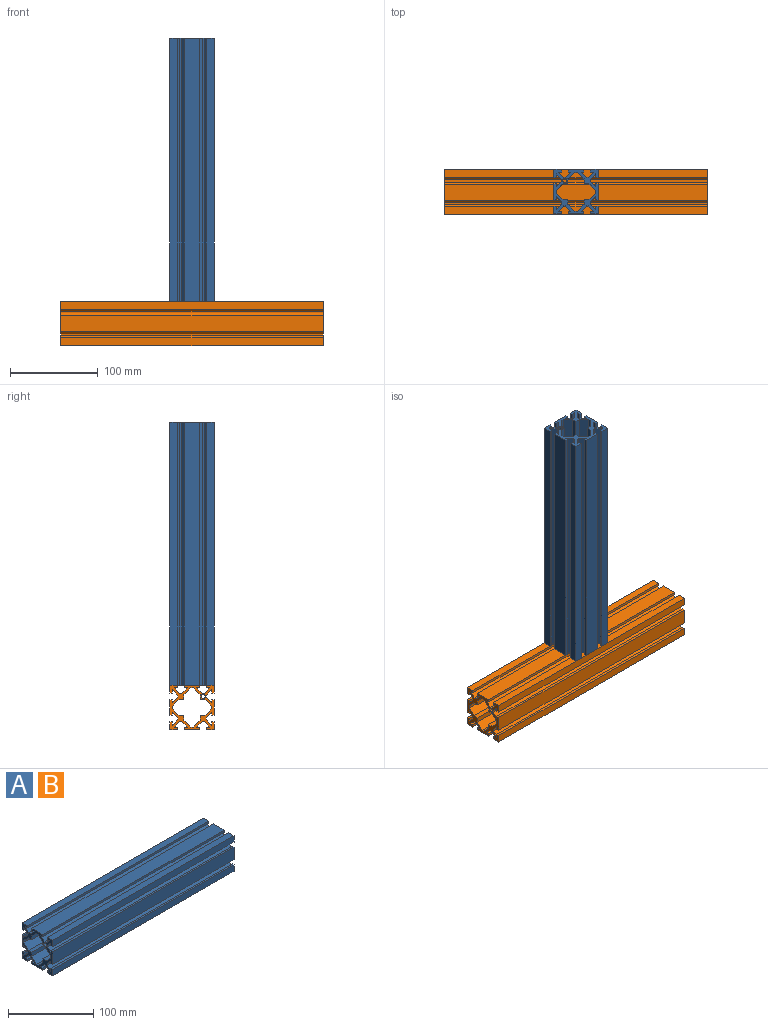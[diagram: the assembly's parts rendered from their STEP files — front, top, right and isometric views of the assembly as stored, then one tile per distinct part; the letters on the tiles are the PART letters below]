
ASSEMBLY  parts=2 mates=2
PART A: 91 faces, bbox 300x50.8x50.8 mm
  f0: plane 300x5.58mm, normal (0,1,0), area 1674mm2, adj f1,f23,f24,f25
  f1: plane 300x7.66mm, normal (0,0.71,-0.71), area 3249.9mm2, adj f0,f2,f24,f25
  f2: plane 300x3mm, normal (0,0,-1), area 900mm2, adj f1,f24,f25,f49
  f3: plane 300x18mm, normal (0,0,1), area 5400mm2, adj f4,f24,f25,f50
  f4: plane 300x3mm, normal (0,-1,0), area 900mm2, adj f3,f5,f24,f25
  f5: plane 300x3.52mm, normal (0,0,-1), area 1056.2mm2, adj f4,f6,f24,f25
  f6: plane 300x6.16mm, normal (0,-0.71,0.71), area 2613.5mm2, adj f5,f7,f24,f25
  f7: plane 300x2.48mm, normal (0,0,1), area 743.8mm2, adj f6,f8,f24,f25
  f8: plane 300x6.16mm, normal (0,0.71,0.71), area 2613.5mm2, adj f7,f9,f24,f25
  f9: plane 300x3.88mm, normal (0,0,-1), area 1163.6mm2, adj f8,f10,f24,f25
  f10: plane 300x3mm, normal (0,1,0), area 900mm2, adj f9,f11,f24,f25
  f11: plane 300x9mm, normal (0,0,1), area 2700mm2, adj f10,f12,f24,f25
  f12: plane 300x9mm, normal (0,-1,0), area 2700mm2, adj f11,f13,f24,f25
  f13: plane 300x3mm, normal (0,0,-1), area 900mm2, adj f12,f14,f24,f25
  f14: plane 300x3.88mm, normal (0,1,0), area 1163.6mm2, adj f13,f15,f24,f25
  f15: plane 300x6.16mm, normal (0,-0.71,-0.71), area 2613.5mm2, adj f14,f16,f24,f25
  f16: plane 300x2.22mm, normal (0,-1,0), area 664.8mm2, adj f15,f17,f24,f25
  f17: plane 300x6.16mm, normal (0,-0.71,0.71), area 2613.5mm2, adj f16,f18,f24,f25
  f18: plane 300x3.26mm, normal (0,1,0), area 977.2mm2, adj f17,f19,f24,f25
  f19: plane 300x3mm, normal (0,0,1), area 900mm2, adj f18,f20,f24,f25
  f20: plane 300x18mm, normal (0,-1,0), area 5400mm2, adj f19,f24,f25,f45
  f21: plane 300x3mm, normal (0,1,0), area 900mm2, adj f22,f24,f25,f46
  f22: plane 300x7.66mm, normal (0,0.71,-0.71), area 3249.9mm2, adj f21,f23,f24,f25
  f23: plane 300x5.58mm, normal (0,0,-1), area 1674mm2, adj f0,f22,f24,f25
  f24: plane 50.8x50.8mm, normal (1,0,0), area 894.8mm2, adj f0,f1,f2,f3,f4,f5,f6,f7
  f25: plane 50.8x50.8mm, normal (-1,0,0), area 894.8mm2, adj f0,f1,f2,f3,f4,f5,f6,f7
  f26: plane 300x5.58mm, normal (0,1,0), area 1674mm2, adj f24,f25,f27,f47
  f27: plane 300x7.66mm, normal (0,0.71,0.71), area 3249.9mm2, adj f24,f25,f26,f28
  f28: plane 300x3mm, normal (0,0,1), area 900mm2, adj f24,f25,f27,f71
  f29: plane 300x18mm, normal (0,0,-1), area 5400mm2, adj f24,f25,f30,f72
  f30: plane 300x3mm, normal (0,-1,0), area 900mm2, adj f24,f25,f29,f31
  f31: plane 300x3.52mm, normal (0,0,1), area 1056.2mm2, adj f24,f25,f30,f32
  f32: plane 300x6.16mm, normal (0,-0.71,-0.71), area 2613.5mm2, adj f24,f25,f31,f33
  f33: plane 300x2.48mm, normal (0,0,-1), area 743.8mm2, adj f24,f25,f32,f34
  f34: plane 300x6.16mm, normal (0,0.71,-0.71), area 2613.5mm2, adj f24,f25,f33,f35
  f35: plane 300x3.88mm, normal (0,0,1), area 1163.6mm2, adj f24,f25,f34,f36
  f36: plane 300x3mm, normal (0,1,0), area 900mm2, adj f24,f25,f35,f37
  f37: plane 300x9mm, normal (0,0,-1), area 2700mm2, adj f24,f25,f36,f38
  f38: plane 300x9mm, normal (0,-1,0), area 2700mm2, adj f24,f25,f37,f39
  f39: plane 300x3mm, normal (0,0,1), area 900mm2, adj f24,f25,f38,f40
  f40: plane 300x3.88mm, normal (0,1,0), area 1163.6mm2, adj f24,f25,f39,f41
  f41: plane 300x6.16mm, normal (0,-0.71,0.71), area 2613.5mm2, adj f24,f25,f40,f42
  f42: plane 300x2.22mm, normal (0,-1,0), area 664.8mm2, adj f24,f25,f41,f43
  f43: plane 300x6.16mm, normal (0,-0.71,-0.71), area 2613.5mm2, adj f24,f25,f42,f44
  f44: plane 300x3.26mm, normal (0,1,0), area 977.2mm2, adj f24,f25,f43,f45
  f45: plane 300x3mm, normal (0,0,-1), area 900mm2, adj f20,f24,f25,f44
  f46: plane 300x7.66mm, normal (0,0.71,0.71), area 3249.9mm2, adj f21,f24,f25,f47
  f47: plane 300x5.58mm, normal (0,0,1), area 1674mm2, adj f24,f25,f26,f46
  f48: plane 300x5.58mm, normal (0,-1,0), area 1674mm2, adj f24,f25,f49,f69
  f49: plane 300x7.66mm, normal (0,-0.71,-0.71), area 3249.9mm2, adj f2,f24,f25,f48
  f50: plane 300x3mm, normal (0,1,0), area 900mm2, adj f3,f24,f25,f51
  f51: plane 300x3.52mm, normal (0,0,-1), area 1056.2mm2, adj f24,f25,f50,f52
  f52: plane 300x6.16mm, normal (0,0.71,0.71), area 2613.5mm2, adj f24,f25,f51,f53
  f53: plane 300x2.48mm, normal (0,0,1), area 743.8mm2, adj f24,f25,f52,f54
  f54: plane 300x6.16mm, normal (0,-0.71,0.71), area 2613.5mm2, adj f24,f25,f53,f55
  f55: plane 300x3.88mm, normal (0,0,-1), area 1163.6mm2, adj f24,f25,f54,f56
  f56: plane 300x3mm, normal (0,-1,0), area 900mm2, adj f24,f25,f55,f57
  f57: plane 300x9mm, normal (0,0,1), area 2700mm2, adj f24,f25,f56,f58
  f58: plane 300x9mm, normal (0,1,0), area 2700mm2, adj f24,f25,f57,f59
  f59: plane 300x3mm, normal (0,0,-1), area 900mm2, adj f24,f25,f58,f60
  f60: plane 300x3.88mm, normal (0,-1,0), area 1163.6mm2, adj f24,f25,f59,f61
  f61: plane 300x6.16mm, normal (0,0.71,-0.71), area 2613.5mm2, adj f24,f25,f60,f62
  f62: plane 300x2.22mm, normal (0,1,0), area 664.8mm2, adj f24,f25,f61,f63
  f63: plane 300x6.16mm, normal (0,0.71,0.71), area 2613.5mm2, adj f24,f25,f62,f64
  f64: plane 300x3.26mm, normal (0,-1,0), area 977.2mm2, adj f24,f25,f63,f65
  f65: plane 300x3mm, normal (0,0,1), area 900mm2, adj f24,f25,f64,f66
  f66: plane 300x18mm, normal (0,1,0), area 5400mm2, adj f24,f25,f65,f87
  f67: plane 300x3mm, normal (0,-1,0), area 900mm2, adj f24,f25,f68,f88
  f68: plane 300x7.66mm, normal (0,-0.71,-0.71), area 3249.9mm2, adj f24,f25,f67,f69
  f69: plane 300x5.58mm, normal (0,0,-1), area 1674mm2, adj f24,f25,f48,f68
  f70: plane 300x5.58mm, normal (0,-1,0), area 1674mm2, adj f24,f25,f71,f89
  f71: plane 300x7.66mm, normal (0,-0.71,0.71), area 3249.9mm2, adj f24,f25,f28,f70
  f72: plane 300x3mm, normal (0,1,0), area 900mm2, adj f24,f25,f29,f73
  f73: plane 300x3.52mm, normal (0,0,1), area 1056.2mm2, adj f24,f25,f72,f74
  f74: plane 300x6.16mm, normal (0,0.71,-0.71), area 2613.5mm2, adj f24,f25,f73,f75
  f75: plane 300x2.48mm, normal (0,0,-1), area 743.8mm2, adj f24,f25,f74,f76
  f76: plane 300x6.16mm, normal (0,-0.71,-0.71), area 2613.5mm2, adj f24,f25,f75,f77
  f77: plane 300x3.88mm, normal (0,0,1), area 1163.6mm2, adj f24,f25,f76,f78
  f78: plane 300x3mm, normal (0,-1,0), area 900mm2, adj f24,f25,f77,f79
  f79: plane 300x9mm, normal (0,0,-1), area 2700mm2, adj f24,f25,f78,f80
  f80: plane 300x9mm, normal (0,1,0), area 2700mm2, adj f24,f25,f79,f81
  f81: plane 300x3mm, normal (0,0,1), area 900mm2, adj f24,f25,f80,f82
  f82: plane 300x3.88mm, normal (0,-1,0), area 1163.6mm2, adj f24,f25,f81,f83
  f83: plane 300x6.16mm, normal (0,0.71,0.71), area 2613.5mm2, adj f24,f25,f82,f84
  f84: plane 300x2.22mm, normal (0,1,0), area 664.8mm2, adj f24,f25,f83,f85
  f85: plane 300x6.16mm, normal (0,0.71,-0.71), area 2613.5mm2, adj f24,f25,f84,f86
  f86: plane 300x3.26mm, normal (0,-1,0), area 977.2mm2, adj f24,f25,f85,f87
  f87: plane 300x3mm, normal (0,0,-1), area 900mm2, adj f24,f25,f66,f86
  f88: plane 300x7.66mm, normal (0,-0.71,0.71), area 3249.9mm2, adj f24,f25,f67,f89
  f89: plane 300x5.58mm, normal (0,0,1), area 1674mm2, adj f24,f25,f70,f88
  f90: cylinder r=2.38mm len=300mm, axis (-1,0,0), area 4490.2mm2, adj f24,f25
PART B: same geometry as A
PLACE A rot(axis=(0.71,0,-0.71),180deg) t=(60.2,16.72,478.93)mm
PLACE B t=(-89.8,16.72,153.53)mm
MATE parallel A.f24 <-> B.f3  axis (0,0,-1) through (69.36,31.46,178.93)mm
MATE parallel B.f20 <-> A.f66  axis (0,-1,0) through (60.2,-8.68,162.53)mm
